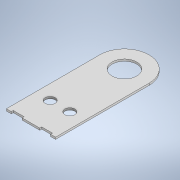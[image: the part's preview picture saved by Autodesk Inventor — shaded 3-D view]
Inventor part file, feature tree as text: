
AUTODESK INVENTOR PART (.ipt)
format: ipt  version: 2022 (Build 260153000, 153)  size: 139,264 bytes
history: native  units: mm
features: sheet_metal_op x1, sketch x1, other x1
ambient origin geometry x8: Origin, YZ Plane, XZ Plane, XY Plane, X Axis, Y Axis, Z Axis, Center Point
bodies: Body1 (feature_tree)
feature tree (3):
  sheet_metal_op  "Face2"
  sketch  "Sketch1"  dims[d0=10.2mm d1=25.0mm d2=2.0mm d3=2.0mm d6=5.0mm d7=11.0mm d8=5.0mm d9=11.0mm d10=50.0mm d12=25.0mm d13=120.0mm d14=29.5mm d16=10.2mm d17=29.5mm d18=20.0mm d19=15.0mm d20=2.0mm]
  other  "Plate2"
